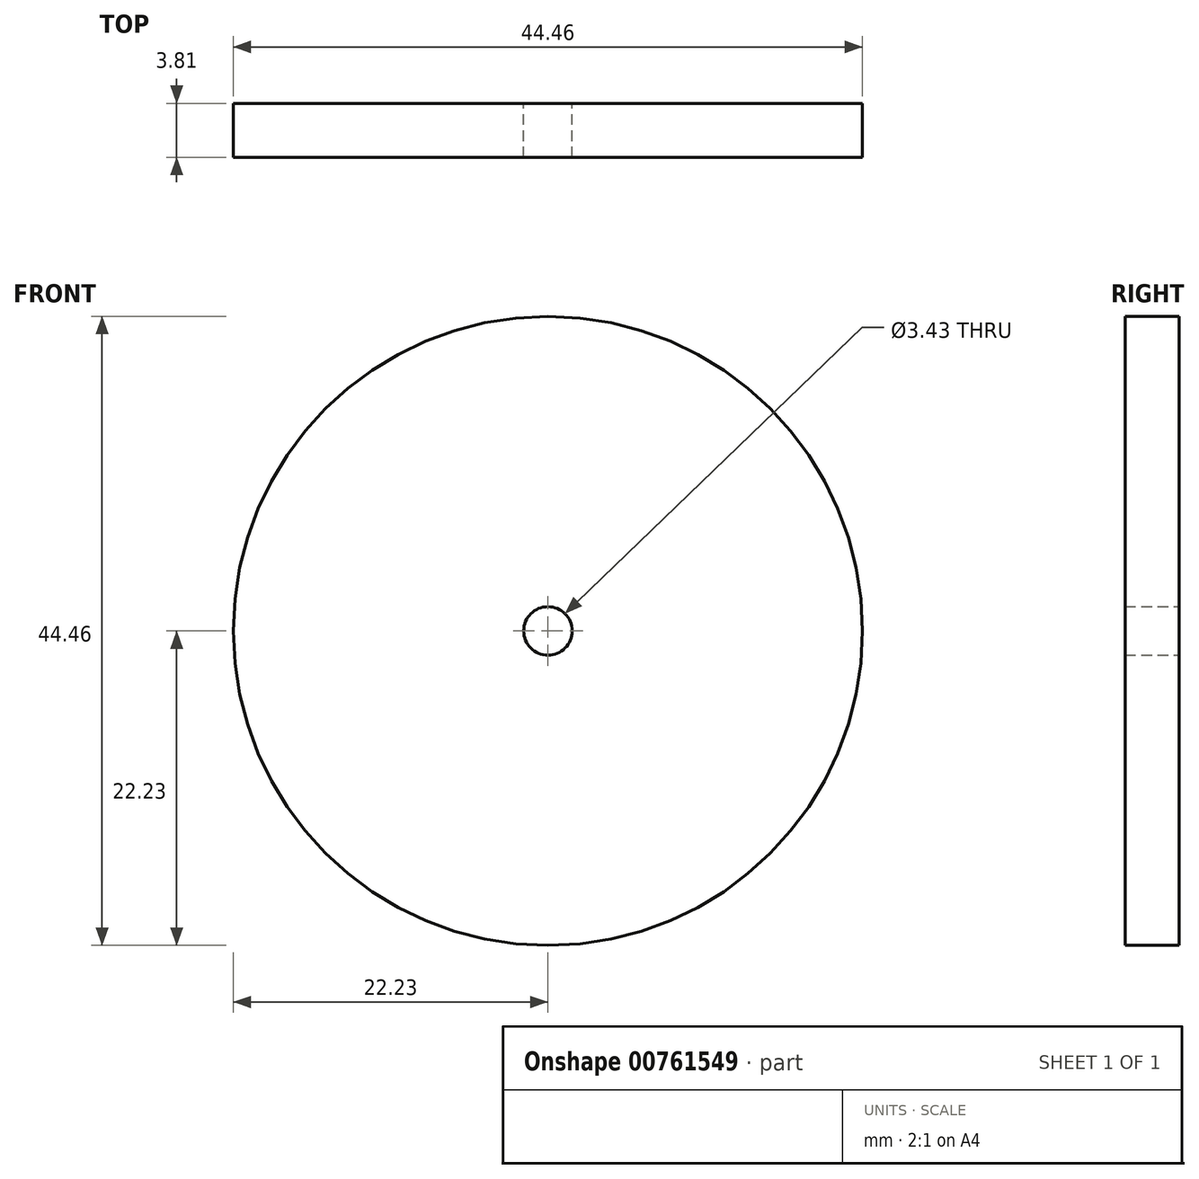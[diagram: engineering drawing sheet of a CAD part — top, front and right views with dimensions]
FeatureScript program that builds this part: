
annotation { "Feature Type Name" : "Feature", "Feature Type Description" : "" }
export const myFeature = defineFeature(function(context is Context, id is Id, definition is map)
    precondition{}
    {
        {
            var Q0;
            Q0=qCreatedBy(makeId("Front.planeOp"),FACE);
            var sketch = newSketch(context, id + "F0", { "sketchPlane" : qUnion([Q0])});
            skCircle(sketch, "E0", {"center": v(0, 0) * mm, "radius": 22.23 * mm});
            skCircle(sketch, "E1", {"center": v(0, 0) * mm, "radius": 1.71 * mm});
            skSolve(sketch);
        }
        {
            var Q0;
            Q0=makeQuery(id+"F0.imprint","IMPRINT",FACE,{"disambiguationData":[TD([[makeQuery(id+"F0.imprint","IMPRINT",EDGE,{"derivedFrom":sQuery(id+"F0.wireOp",EDGE,"E0")}),1.0]])]});
            extrude(context, id + "F1", {"entities" : qUnion([Q0]), "depth" : 3.8 * mm, "offsetDistance" : 25.4 * mm});
        }
    });
